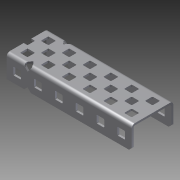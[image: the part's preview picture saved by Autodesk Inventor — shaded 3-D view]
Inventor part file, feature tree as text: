
AUTODESK INVENTOR PART (.ipt)
format: ipt  version: 2014 SP1 (Build 180222100, 222)  size: 696,320 bytes
history: native  units: in
note: dims shown in document units (in); Inventor stores cm internally (conversion verified against a paired STEP export)
features: other x1, imported_body x1, extrude x1, sketch x1
ambient origin geometry x8: Origin, YZ Plane, XZ Plane, XY Plane, X Axis, Y Axis, Z Axis, Center Point
bodies: Body1 (feature_tree)
feature tree (4):
  parser-record x1  (decoder bookkeeping rows leaked as tree rows — omitted from the tree; the rows remain in map.json)
  imported_body  "Base1"
  extrude  "Extrusion1"  Depth=1.0in TaperAngle=0.0deg
  sketch  "Sketch2"  dims[d0=2.0in d1=1.0in d2=0.0in]
